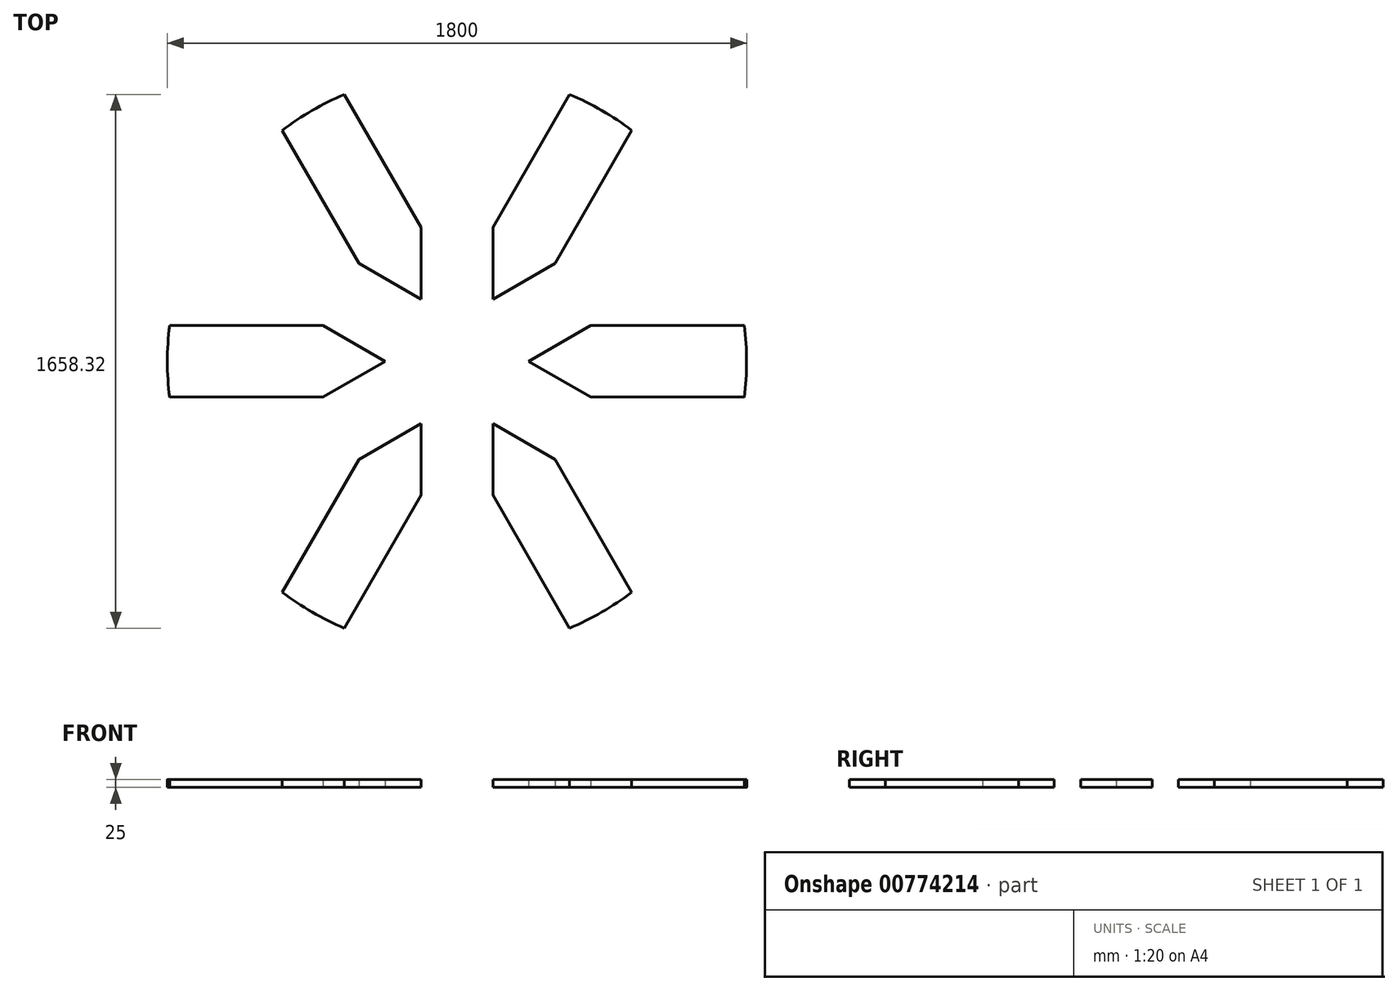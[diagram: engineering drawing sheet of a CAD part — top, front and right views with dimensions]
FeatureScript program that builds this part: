
annotation { "Feature Type Name" : "Feature", "Feature Type Description" : "" }
export const myFeature = defineFeature(function(context is Context, id is Id, definition is map)
    precondition{}
    {
        {
            var Q0;
            Q0=qCreatedBy(makeId("Top.planeOp"),FACE);
            var sketch = newSketch(context, id + "F0", { "sketchPlane" : qUnion([Q0])});
            skCircle(sketch, "E0", {"center": v(0, 0) * mm, "radius": 700 * mm});
            skCircle(sketch, "E1", {"center": v(0, 0) * mm, "radius": 900 * mm});
            skLineSegment(sketch, "E2", {"start": v(-350, 606.22) * mm, "end": v(-350, 829.16) * mm, "construction": true});
            skLineSegment(sketch, "E3", {"start": v(350, 606.22) * mm, "end": v(350, 829.16) * mm, "construction": true});
            skLineSegment(sketch, "E4", {"start": v(-350, 829.16) * mm, "end": v(0, 222.94) * mm});
            skLineSegment(sketch, "E5", {"start": v(0, 222.94) * mm, "end": v(375.18, 872.78) * mm});
            skCircle(sketch, "E6", {"center": v(0, 0) * mm, "radius": 950 * mm});
            skLineSegment(sketch, "E7", {"start": v(-350, 829.16) * mm, "end": v(-375.18, 872.78) * mm});
            skLineSegment(sketch, "E8.1.0", {"start": v(-943.44, 111.47) * mm, "end": v(-193.07, 111.47) * mm});
            skLineSegment(sketch, "E8.1.1", {"start": v(-193.07, 111.47) * mm, "end": v(-568.25, 761.3) * mm});
            skLineSegment(sketch, "E8.2.0", {"start": v(-568.25, -761.3) * mm, "end": v(-193.07, -111.47) * mm});
            skLineSegment(sketch, "E8.2.1", {"start": v(-193.07, -111.47) * mm, "end": v(-943.44, -111.47) * mm});
            skLineSegment(sketch, "E8.3.0", {"start": v(375.18, -872.78) * mm, "end": v(0, -222.94) * mm});
            skLineSegment(sketch, "E8.3.1", {"start": v(0, -222.94) * mm, "end": v(-375.18, -872.78) * mm});
            skLineSegment(sketch, "E8.4.0", {"start": v(943.44, -111.47) * mm, "end": v(193.07, -111.47) * mm});
            skLineSegment(sketch, "E8.4.1", {"start": v(193.07, -111.47) * mm, "end": v(568.25, -761.3) * mm});
            skLineSegment(sketch, "E8.5.0", {"start": v(568.25, 761.3) * mm, "end": v(193.07, 111.47) * mm});
            skLineSegment(sketch, "E8.5.1", {"start": v(193.07, 111.47) * mm, "end": v(943.44, 111.47) * mm});
            skPoint(sketch, "E9.orphan", {"position": v(-893.07, 111.47) * mm});
            skPoint(sketch, "E10.orphan", {"position": v(-543.07, -717.69) * mm});
            skPoint(sketch, "E11.orphan", {"position": v(350, -829.16) * mm});
            skPoint(sketch, "E12.orphan", {"position": v(893.07, -111.47) * mm});
            skPoint(sketch, "E13.orphan", {"position": v(543.07, 717.69) * mm});
            skCircle(sketch, "E14", {"center": v(0, 0) * mm, "radius": 222.94 * mm, "construction": true});
            skLineSegment(sketch, "E15", {"start": v(-193.07, 111.47) * mm, "end": v(0, 222.94) * mm, "construction": true});
            skLineSegment(sketch, "E16", {"start": v(-568.25, 761.3) * mm, "end": v(-375.18, 872.78) * mm, "construction": true});
            skLineSegment(sketch, "E17", {"start": v(-96.54, 167.2) * mm, "end": v(-475, 822.72) * mm, "construction": true});
            skLineSegment(sketch, "E18", {"start": v(-111.47, 193.07) * mm, "end": v(-304.54, 304.54) * mm});
            skLineSegment(sketch, "E19", {"start": v(-111.47, 193.07) * mm, "end": v(-111.47, 416) * mm});
            skLineSegment(sketch, "E20", {"start": v(-111.47, 193.07) * mm, "end": v(-208, 137.34) * mm, "construction": true});
            skLineSegment(sketch, "E21.1.0", {"start": v(-222.94, 0) * mm, "end": v(-416, -111.47) * mm});
            skLineSegment(sketch, "E21.1.1", {"start": v(-222.94, 0) * mm, "end": v(-416, 111.47) * mm});
            skLineSegment(sketch, "E21.2.0", {"start": v(-111.47, -193.07) * mm, "end": v(-111.47, -416) * mm});
            skLineSegment(sketch, "E21.2.1", {"start": v(-111.47, -193.07) * mm, "end": v(-304.54, -304.54) * mm});
            skLineSegment(sketch, "E21.3.0", {"start": v(111.47, -193.07) * mm, "end": v(304.54, -304.54) * mm});
            skLineSegment(sketch, "E21.3.1", {"start": v(111.47, -193.07) * mm, "end": v(111.47, -416) * mm});
            skLineSegment(sketch, "E21.4.0", {"start": v(222.94, 0) * mm, "end": v(416, 111.47) * mm});
            skLineSegment(sketch, "E21.4.1", {"start": v(222.94, 0) * mm, "end": v(416, -111.47) * mm});
            skLineSegment(sketch, "E21.5.0", {"start": v(111.47, 193.07) * mm, "end": v(111.47, 416) * mm});
            skLineSegment(sketch, "E21.5.1", {"start": v(111.47, 193.07) * mm, "end": v(304.54, 304.54) * mm});
            skSolve(sketch);
        }
        {
            var Q0;
            {var subQ0=sQuery(id+"F0.wireOp",EDGE,"E21.1.0");Q0=makeQuery(id+"F0.imprint","IMPRINT",FACE,{"disambiguationData":[TD([[makeQuery(id+"F0.imprint","IMPRINT",EDGE,{"derivedFrom":subQ0}),-1.0]])]});}
            var Q1;
            {var subQ0=sQuery(id+"F0.wireOp",EDGE,"E8.1.0");var subQ1=sQuery(id+"F0.wireOp",EDGE,"E0");var subQ2=makeQuery(id+"F0.imprint","INTERSECT",VERTEX,{"derivedFrom":[subQ1,subQ0]});Q1=makeQuery(id+"F0.imprint","IMPRINT",FACE,{"disambiguationData":[TD([[makeQuery(id+"F0.imprint","IMPRINT",EDGE,{"disambiguationData":[TD([[subQ2,-1.0]])],"derivedFrom":subQ1}),-1.0]])]});}
            var Q2;
            {var subQ0=sQuery(id+"F0.wireOp",EDGE,"E8.2.0");var subQ1=sQuery(id+"F0.wireOp",EDGE,"E0");var subQ2=makeQuery(id+"F0.imprint","INTERSECT",VERTEX,{"derivedFrom":[subQ1,subQ0]});Q2=makeQuery(id+"F0.imprint","IMPRINT",FACE,{"disambiguationData":[TD([[makeQuery(id+"F0.imprint","IMPRINT",EDGE,{"disambiguationData":[TD([[subQ2,-1.0]])],"derivedFrom":subQ1}),-1.0]])]});}
            var Q3;
            {var subQ0=sQuery(id+"F0.wireOp",EDGE,"E21.2.0");Q3=makeQuery(id+"F0.imprint","IMPRINT",FACE,{"disambiguationData":[TD([[makeQuery(id+"F0.imprint","IMPRINT",EDGE,{"derivedFrom":subQ0}),-1.0]])]});}
            var Q4;
            {var subQ0=sQuery(id+"F0.wireOp",EDGE,"E21.3.0");Q4=makeQuery(id+"F0.imprint","IMPRINT",FACE,{"disambiguationData":[TD([[makeQuery(id+"F0.imprint","IMPRINT",EDGE,{"derivedFrom":subQ0}),-1.0]])]});}
            var Q5;
            {var subQ0=sQuery(id+"F0.wireOp",EDGE,"E21.4.0");Q5=makeQuery(id+"F0.imprint","IMPRINT",FACE,{"disambiguationData":[TD([[makeQuery(id+"F0.imprint","IMPRINT",EDGE,{"derivedFrom":subQ0}),-1.0]])]});}
            var Q6;
            {var subQ0=sQuery(id+"F0.wireOp",EDGE,"E8.5.1");var subQ1=sQuery(id+"F0.wireOp",EDGE,"E0");var subQ2=makeQuery(id+"F0.imprint","INTERSECT",VERTEX,{"derivedFrom":[subQ1,subQ0]});Q6=makeQuery(id+"F0.imprint","IMPRINT",FACE,{"disambiguationData":[TD([[makeQuery(id+"F0.imprint","IMPRINT",EDGE,{"disambiguationData":[TD([[subQ2,1.0]])],"derivedFrom":subQ1}),-1.0]])]});}
            var Q7;
            {var subQ0=sQuery(id+"F0.wireOp",EDGE,"E21.5.0");Q7=makeQuery(id+"F0.imprint","IMPRINT",FACE,{"disambiguationData":[TD([[makeQuery(id+"F0.imprint","IMPRINT",EDGE,{"derivedFrom":subQ0}),-1.0]])]});}
            var Q8;
            {var subQ0=sQuery(id+"F0.wireOp",EDGE,"E8.5.0");var subQ1=sQuery(id+"F0.wireOp",EDGE,"E0");var subQ2=makeQuery(id+"F0.imprint","INTERSECT",VERTEX,{"derivedFrom":[subQ1,subQ0]});Q8=makeQuery(id+"F0.imprint","IMPRINT",FACE,{"disambiguationData":[TD([[makeQuery(id+"F0.imprint","IMPRINT",EDGE,{"disambiguationData":[TD([[subQ2,-1.0]])],"derivedFrom":subQ1}),-1.0]])]});}
            var Q9;
            {var subQ0=sQuery(id+"F0.wireOp",EDGE,"E18");Q9=makeQuery(id+"F0.imprint","IMPRINT",FACE,{"disambiguationData":[TD([[makeQuery(id+"F0.imprint","IMPRINT",EDGE,{"derivedFrom":subQ0}),-1.0]])]});}
            var Q10;
            {var subQ0=sQuery(id+"F0.wireOp",EDGE,"E4");var subQ1=sQuery(id+"F0.wireOp",EDGE,"E0");var subQ2=makeQuery(id+"F0.imprint","INTERSECT",VERTEX,{"derivedFrom":[subQ1,subQ0]});Q10=makeQuery(id+"F0.imprint","IMPRINT",FACE,{"disambiguationData":[TD([[makeQuery(id+"F0.imprint","IMPRINT",EDGE,{"disambiguationData":[TD([[subQ2,-1.0]])],"derivedFrom":subQ1}),-1.0]])]});}
            var Q11;
            {var subQ0=sQuery(id+"F0.wireOp",EDGE,"E8.3.0");var subQ1=sQuery(id+"F0.wireOp",EDGE,"E0");var subQ2=makeQuery(id+"F0.imprint","INTERSECT",VERTEX,{"derivedFrom":[subQ1,subQ0]});Q11=makeQuery(id+"F0.imprint","IMPRINT",FACE,{"disambiguationData":[TD([[makeQuery(id+"F0.imprint","IMPRINT",EDGE,{"disambiguationData":[TD([[subQ2,-1.0]])],"derivedFrom":subQ1}),-1.0]])]});}
            extrude(context, id + "F1", {"entities" : qUnion([Q0, Q1, Q2, Q3, Q4, Q5, Q6, Q7, Q8, Q9, Q10, Q11]), "depth" : 25 * mm, "offsetDistance" : 25 * mm});
        }
    });
